FCSTD DOCUMENT  (FreeCAD 0.18.3R)
Label: 20191106.stl
License: All rights reserved
LicenseURL: http://en.wikipedia.org/wiki/All_rights_reserved
objects: Part::Feature×3, Mesh::Feature×1, Part::Box×1, Part::FeaturePython×1, Part::Part2DObjectPython×1, Part::Extrusion×1, Part::Cut×1, Part::Fuse×1
note: 9 computed .brp shape members not serialized (recipe doc carries the construction recipe); baked Part::Feature solids carry a one-line shape summary decoded from their .brp

FEATURE [Mesh::Feature] moai
  Placement = pos=(0,0,0) rot=(1,0,0;4.71239rad)
FEATURE [Part::Box] Box  label="innerCube"
  AttacherType = Attacher::AttachEngine3D
  Height = 20
  Length = 70
  Placement = pos=(0,-195,0) rot=(0,0,1;0rad)
  Width = 70
FEATURE [Part::Feature] moai001
  shape: large baked B-rep (44 MB .brp); summary skipped
FEATURE [Part::Feature] moai001_solid  label="moai001 (Solid)"
  shape: large baked B-rep (44 MB .brp); summary skipped
FEATURE [Part::Feature] moai001_solid001  label="moai001 (Solid)001"
  shape: large baked B-rep (44 MB .brp); summary skipped
FEATURE [Part::FeaturePython] Clone  label="moai001 (Solid)002"  # Draft clone (typed FeaturePython)
  AttacherType = Attacher::AttachEngine3D
  Fuse = false
  Objects = -> [moai001_solid001]
  Placement = pos=(35,-167,-15) rot=(0,0,1;0rad)
  Scale = (0.25,0.25,0.25)
FEATURE [Part::Part2DObjectPython] ShapeString001  # Draft 2D object (typed FeaturePython)
  FontFile = <userpath>/_workspace/moai_plate/Arial.ttf
  Placement = pos=(16.5364,-160.98,20) rot=(0,0,1;0rad)
  Size = 5
  String = 20191106.stl
  Tracking = 0
FEATURE [Part::Extrusion] Extrude
  Base = -> ShapeString001
  Dir = (0,0,1)
  DirMode = 0
  FaceMakerClass = Part::FaceMakerBullseye
  LengthFwd = 5
  LengthRev = 0
  Placement = pos=(0,0,-2) rot=(0,0,1;0rad)
  Solid = false
  Symmetric = false
FEATURE [Part::Cut] Cut
  Base = -> Box
  Tool = -> Extrude
FEATURE [Part::Fuse] Fusion
  Base = -> Clone
  Tool = -> Cut
